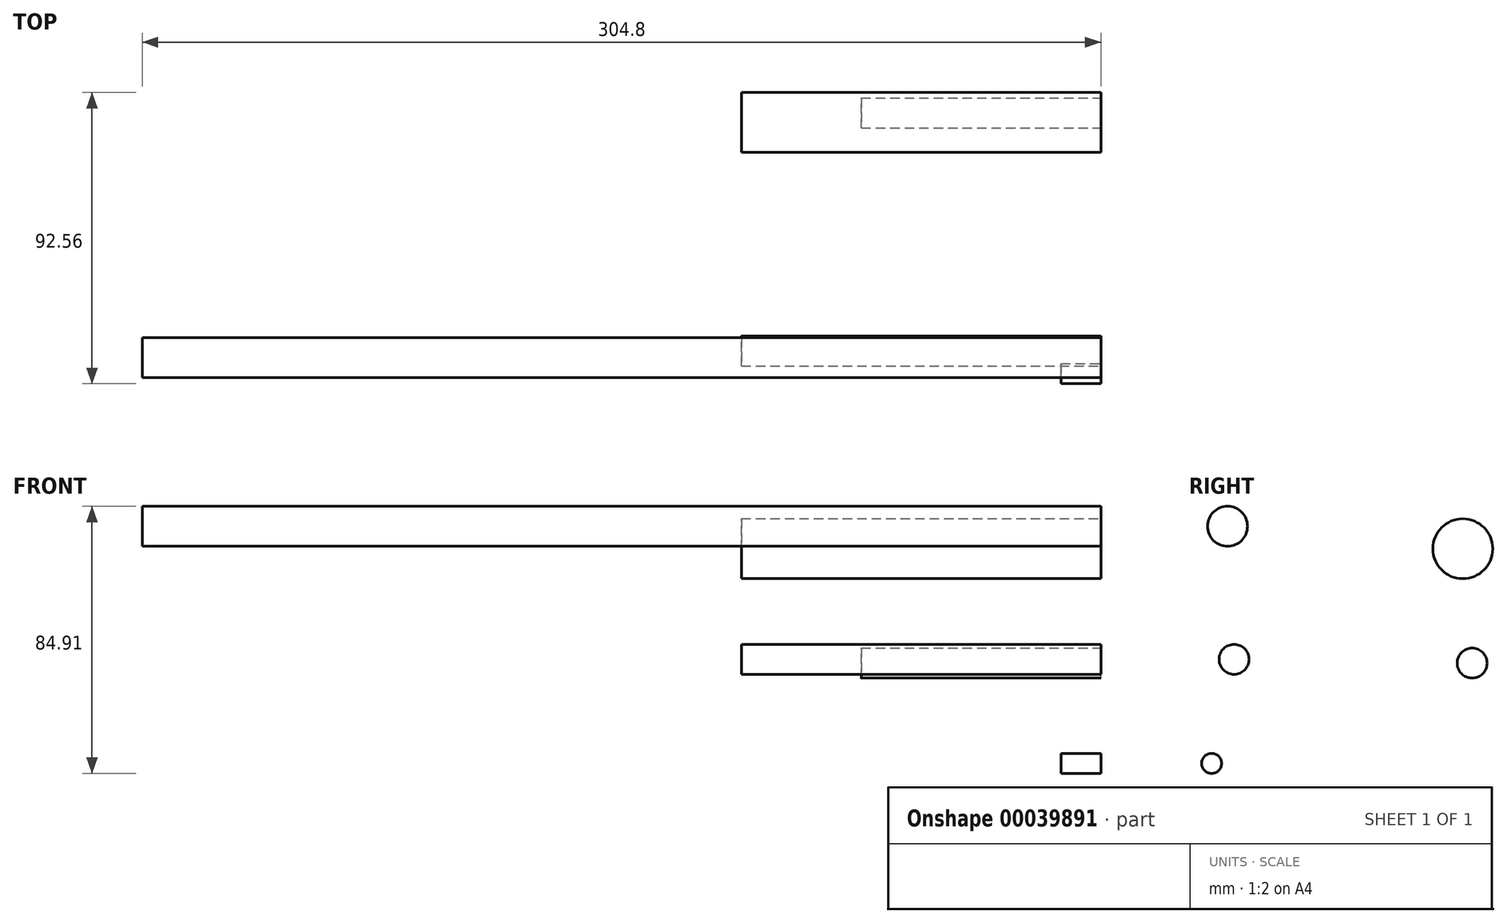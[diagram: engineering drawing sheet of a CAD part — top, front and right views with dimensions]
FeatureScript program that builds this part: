
annotation { "Feature Type Name" : "Feature", "Feature Type Description" : "" }
export const myFeature = defineFeature(function(context is Context, id is Id, definition is map)
    precondition{}
    {
        {
            var Q0;
            Q0=qCreatedBy(makeId("Right.planeOp"),FACE);
            var sketch = newSketch(context, id + "F0", { "sketchPlane" : qUnion([Q0])});
            skCircle(sketch, "E0", {"center": v(-36.06, 58.85) * mm, "radius": 6.35 * mm});
            skSolve(sketch);
        }
        {
            var Q0;
            Q0=makeQuery(id+"F0.imprint","IMPRINT",FACE,{"disambiguationData":[TD([[makeQuery(id+"F0.imprint","IMPRINT",EDGE,{"derivedFrom":sQuery(id+"F0.wireOp",EDGE,"E0")}),1.0]])]});
            extrude(context, id + "F1", {"entities" : qUnion([Q0]), "oppositeDirection" : true, "depth" : 304.8 * mm});
        }
        {
            var Q0;
            Q0=qCreatedBy(makeId("Right.planeOp"),FACE);
            var sketch = newSketch(context, id + "F2", { "sketchPlane" : qUnion([Q0])});
            skCircle(sketch, "E1", {"center": v(38.74, 51.7) * mm, "radius": 9.53 * mm});
            skSolve(sketch);
        }
        {
            var Q0;
            Q0=makeQuery(id+"F2.imprint","IMPRINT",FACE,{"disambiguationData":[TD([[makeQuery(id+"F2.imprint","IMPRINT",EDGE,{"derivedFrom":sQuery(id+"F2.wireOp",EDGE,"E1")}),1.0]])]});
            extrude(context, id + "F3", {"entities" : qUnion([Q0]), "oppositeDirection" : true, "depth" : 114.3 * mm});
        }
        {
            var Q0;
            Q0=qCreatedBy(makeId("Right.planeOp"),FACE);
            var sketch = newSketch(context, id + "F4", { "sketchPlane" : qUnion([Q0])});
            skCircle(sketch, "E2", {"center": v(-33.97, 16.54) * mm, "radius": 4.76 * mm});
            skSolve(sketch);
        }
        {
            var Q0;
            Q0 = qSketchRegion(id + "F4", true);
            extrude(context, id + "F5", {"entities" : qUnion([Q0]), "oppositeDirection" : true, "depth" : 114.3 * mm});
        }
        {
            var Q0;
            Q0=qCreatedBy(makeId("Right.planeOp"),FACE);
            var sketch = newSketch(context, id + "F6", { "sketchPlane" : qUnion([Q0])});
            skCircle(sketch, "E3", {"center": v(41.72, 15.35) * mm, "radius": 4.76 * mm});
            skSolve(sketch);
        }
        {
            var Q0;
            Q0=makeQuery(id+"F6.imprint","IMPRINT",FACE,{"disambiguationData":[TD([[makeQuery(id+"F6.imprint","IMPRINT",EDGE,{"derivedFrom":sQuery(id+"F6.wireOp",EDGE,"E3")}),1.0]])]});
            extrude(context, id + "F7", {"entities" : qUnion([Q0]), "oppositeDirection" : true, "depth" : 76.2 * mm});
        }
        {
            var Q0;
            Q0=qCreatedBy(makeId("Right.planeOp"),FACE);
            var sketch = newSketch(context, id + "F8", { "sketchPlane" : qUnion([Q0])});
            skCircle(sketch, "E4", {"center": v(-41.12, -16.54) * mm, "radius": 3.18 * mm});
            skSolve(sketch);
        }
        {
            var Q0;
            Q0 = qSketchRegion(id + "F8", true);
            extrude(context, id + "F9", {"entities" : qUnion([Q0]), "oppositeDirection" : true, "depth" : 12.7 * mm});
        }
    });
